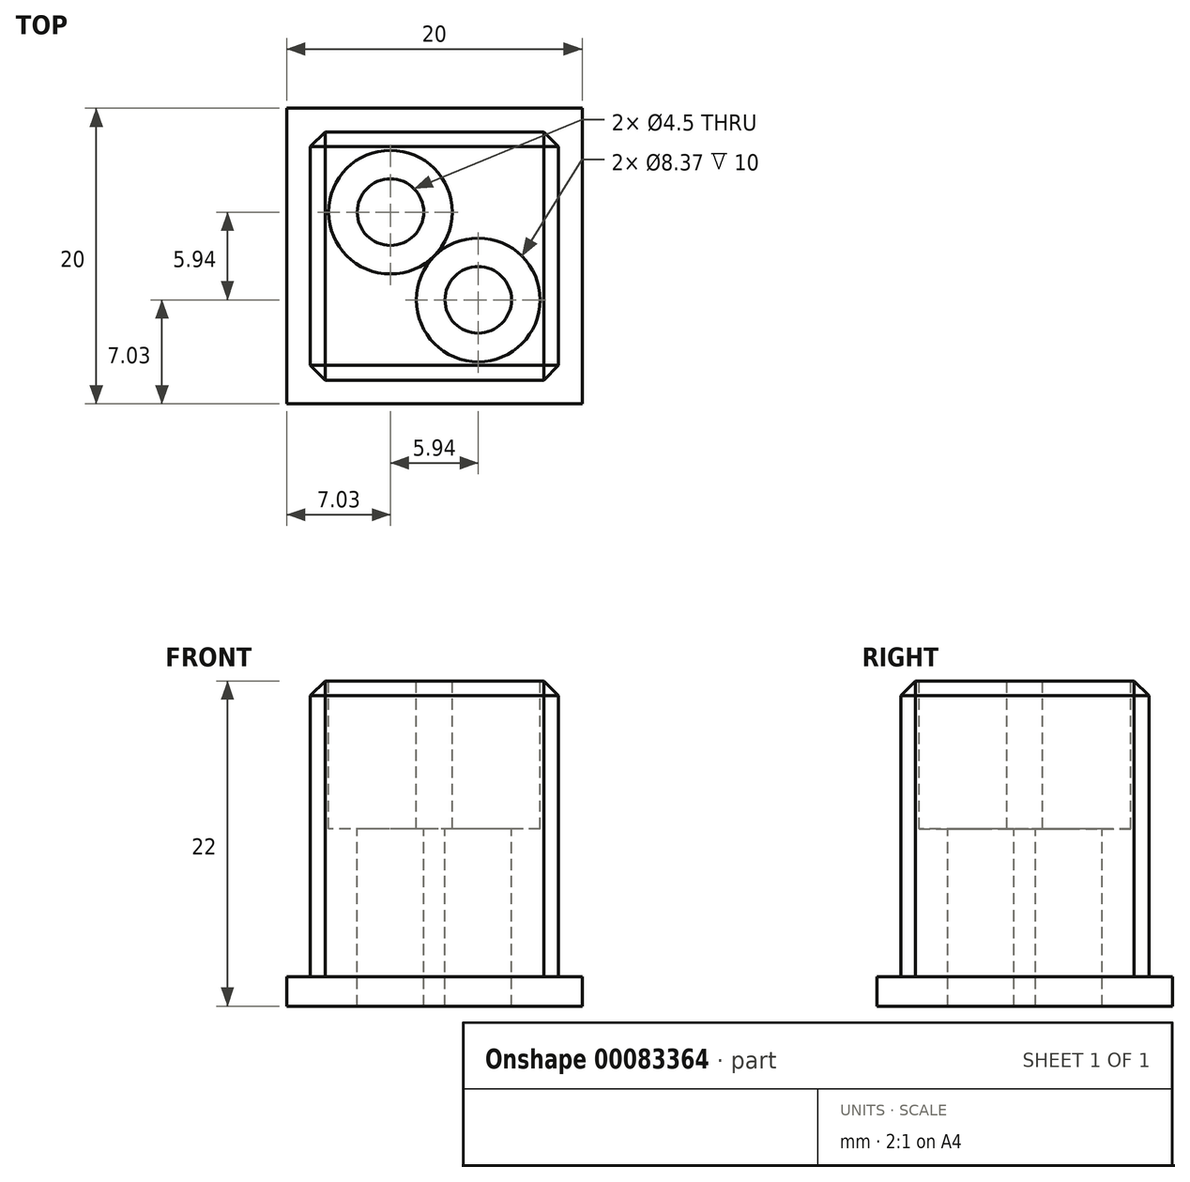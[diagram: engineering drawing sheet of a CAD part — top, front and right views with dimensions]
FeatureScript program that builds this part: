
annotation { "Feature Type Name" : "Feature", "Feature Type Description" : "" }
export const myFeature = defineFeature(function(context is Context, id is Id, definition is map)
    precondition{}
    {
        {
            var Q0;
            Q0=qCreatedBy(makeId("Top.planeOp"),FACE);
            var sketch = newSketch(context, id + "F0", { "sketchPlane" : qUnion([Q0])});
            skLineSegment(sketch, "E0", {"start": v(5, 20) * mm, "end": v(5, 0) * mm});
            skLineSegment(sketch, "E1", {"start": v(25, 20) * mm, "end": v(25, 0) * mm});
            skLineSegment(sketch, "E2", {"start": v(5, 20) * mm, "end": v(25, 20) * mm});
            skLineSegment(sketch, "E3", {"start": v(25, 0) * mm, "end": v(5, 0) * mm});
            skSolve(sketch);
        }
        {
            var Q0;
            {var subQ1=sQuery(id+"F0.wireOp",EDGE,"E0");Q0=makeQuery(id+"F0.imprint","IMPRINT",FACE,{"disambiguationData":[TD([[makeQuery(id+"F0.imprint","IMPRINT",EDGE,{"derivedFrom":subQ1}),1.0]])]});}
            extrude(context, id + "F1", {"entities" : qUnion([Q0]), "depth" : 2 * mm});
        }
        {
            var Q0;
            Q0=makeQuery(id+"F1.opExtrude","CAP_FACE",FACE,{"disambiguationData":[OSD([sQuery(id+"F0.wireOp",EDGE,"cecbb5cf-455c-4329-a757-5271d48d16f4.bottom"),sQuery(id+"F0.wireOp",EDGE,"cecbb5cf-455c-4329-a757-5271d48d16f4.top"),sQuery(id+"F0.wireOp",EDGE,"E0"),sQuery(id+"F0.wireOp",EDGE,"E1")])],"isStart":false});
            var sketch = newSketch(context, id + "F2", { "sketchPlane" : qUnion([Q0])});
            skLineSegment(sketch, "E4.0", {"start": v(6.6, 18.4) * mm, "end": v(23.4, 18.4) * mm});
            skLineSegment(sketch, "E4.1", {"start": v(6.6, 18.4) * mm, "end": v(6.6, 1.6) * mm});
            skLineSegment(sketch, "E4.2", {"start": v(23.4, 1.6) * mm, "end": v(6.6, 1.6) * mm});
            skLineSegment(sketch, "E4.3", {"start": v(23.4, 18.4) * mm, "end": v(23.4, 1.6) * mm});
            skSolve(sketch);
        }
        {
            var Q0;
            Q0=makeQuery(id+"F2.imprint","IMPRINT",FACE,{"disambiguationData":[TD([[makeQuery(id+"F2.imprint","IMPRINT",EDGE,{"derivedFrom":sQuery(id+"F2.wireOp",EDGE,"E4.0")}),-1.0]])]});
            extrude(context, id + "F3", {"entities" : qUnion([Q0]), "operationType" : NewBodyOperationType.ADD, "depth" : 20 * mm});
        }
        {
            var Q0;
            Q0=makeQuery(id+"F3.opExtrude","SWEPT_EDGE",EDGE,{"disambiguationData":[OSD([sQuery(id+"F2.wireOp",EDGE,"E4.0"),sQuery(id+"F2.wireOp",EDGE,"E4.1")])]});
            var Q1;
            Q1=makeQuery(id+"F3.opExtrude","CAP_EDGE",EDGE,{"disambiguationData":[OSD([sQuery(id+"F2.wireOp",EDGE,"E4.1")])],"isStart":false});
            var Q2;
            Q2=makeQuery(id+"F3.opExtrude","CAP_EDGE",EDGE,{"disambiguationData":[OSD([sQuery(id+"F2.wireOp",EDGE,"E4.0")])],"isStart":false});
            var Q3;
            Q3=makeQuery(id+"F3.opExtrude","SWEPT_EDGE",EDGE,{"disambiguationData":[OSD([sQuery(id+"F2.wireOp",EDGE,"E4.0"),sQuery(id+"F2.wireOp",EDGE,"E4.3")])]});
            var Q4;
            Q4=makeQuery(id+"F3.opExtrude","CAP_EDGE",EDGE,{"disambiguationData":[OSD([sQuery(id+"F2.wireOp",EDGE,"E4.3")])],"isStart":false});
            var Q5;
            Q5=makeQuery(id+"F3.opExtrude","CAP_EDGE",EDGE,{"disambiguationData":[OSD([sQuery(id+"F2.wireOp",EDGE,"E4.2")])],"isStart":false});
            var Q6;
            Q6=makeQuery(id+"F3.opExtrude","SWEPT_EDGE",EDGE,{"disambiguationData":[OSD([sQuery(id+"F2.wireOp",EDGE,"E4.1"),sQuery(id+"F2.wireOp",EDGE,"E4.2")])]});
            var Q7;
            Q7=makeQuery(id+"F3.opExtrude","SWEPT_EDGE",EDGE,{"disambiguationData":[OSD([sQuery(id+"F2.wireOp",EDGE,"E4.2"),sQuery(id+"F2.wireOp",EDGE,"E4.3")])]});
            chamfer(context, id + "F4", {"entities" : qUnion([Q0, Q1, Q2, Q3, Q4, Q5, Q6, Q7]), "width" : 1 * mm, "tangentPropagation" : true});
        }
        {
            var Q0;
            Q0=makeQuery(id+"F3.opExtrude","CAP_FACE",FACE,{"disambiguationData":[OSD([sQuery(id+"F2.wireOp",EDGE,"E4.0"),sQuery(id+"F2.wireOp",EDGE,"E4.1"),sQuery(id+"F2.wireOp",EDGE,"E4.2"),sQuery(id+"F2.wireOp",EDGE,"E4.3")])],"isStart":false});
            var sketch = newSketch(context, id + "F5", { "sketchPlane" : qUnion([Q0])});
            skLineSegment(sketch, "E5", {"start": v(7.6, 17.4) * mm, "end": v(22.4, 2.6) * mm, "construction": true});
            skPoint(sketch, "E6", {"position": v(15, 10) * mm});
            skPoint(sketch, "E7", {"position": v(12.03, 12.97) * mm});
            skPoint(sketch, "E8", {"position": v(17.97, 7.03) * mm});
            skSolve(sketch);
        }
        {
            var Q0;
            Q0=sQuery(id+"F5.wireOp",VERTEX,"E7");
            var Q1;
            Q1=sQuery(id+"F5.wireOp",VERTEX,"E8");
            var Q2;
            Q2=makeQuery(id+"F1.opExtrude","SWEPT_BODY",BODY,{"disambiguationData":[OSD([sQuery(id+"F0.wireOp",EDGE,"E0"),sQuery(id+"F0.wireOp",EDGE,"E1"),sQuery(id+"F0.wireOp",EDGE,"E2"),sQuery(id+"F0.wireOp",EDGE,"E3")])]});
            hole(context, id + "F6", {"style" : HoleStyle.C_BORE, "endStyle" : HoleEndStyle.THROUGH, "holeDiameter" : 4.5 * mm, "cBoreDiameter" : 8.37 * mm, "cBoreDepth" : 10 * mm, "startFromSketch" : true, "locations" : qUnion([Q0, Q1]), "scope" : qUnion([Q2]), "isTappedThrough" : true});
        }
    });
